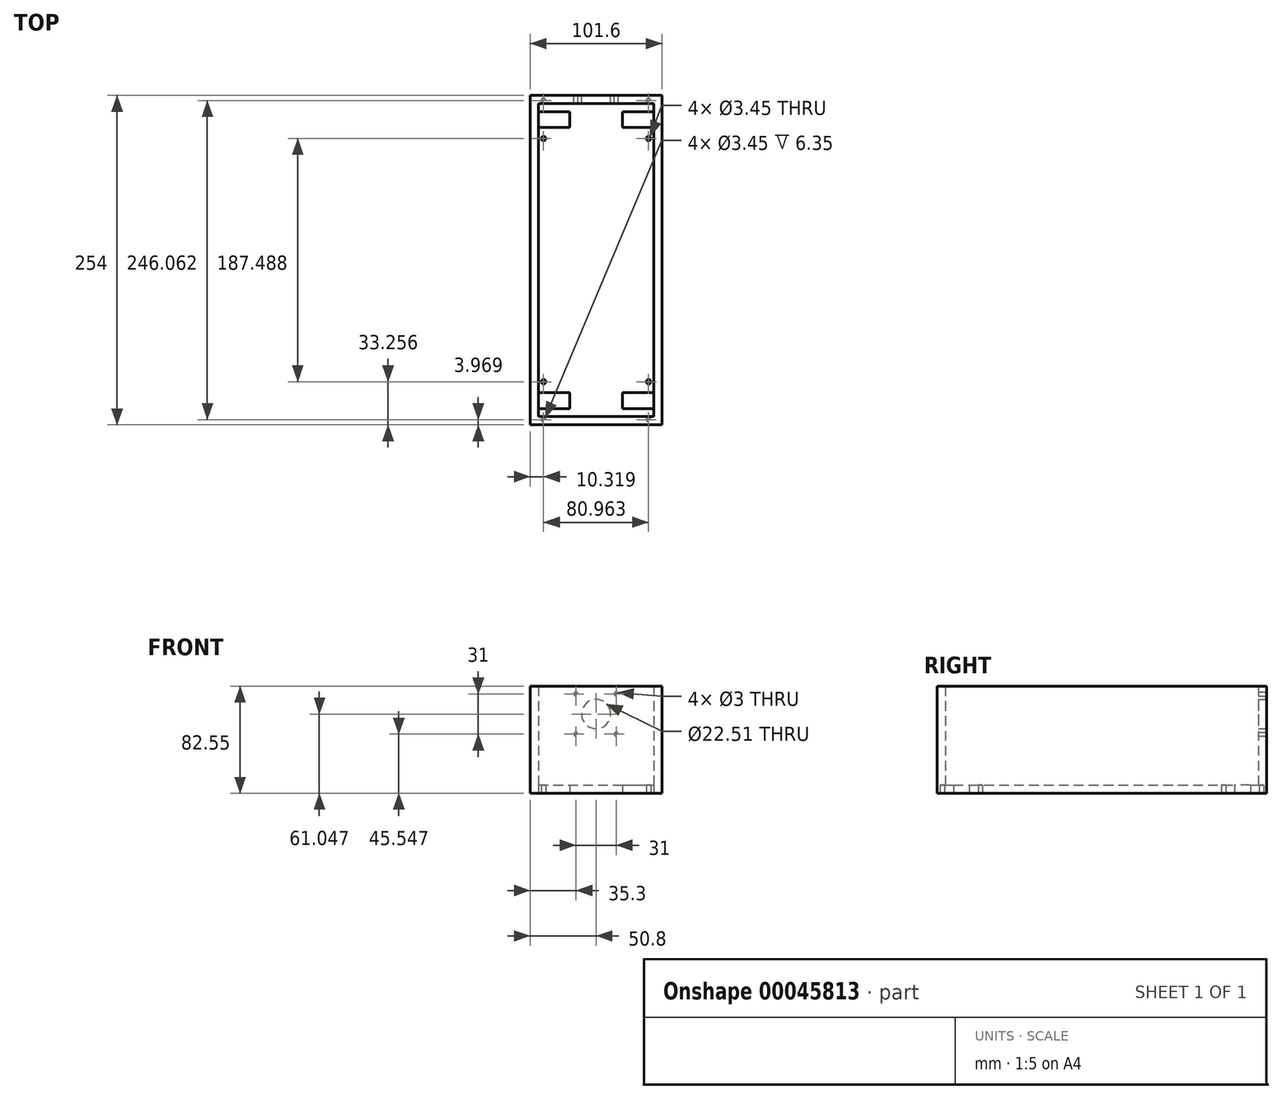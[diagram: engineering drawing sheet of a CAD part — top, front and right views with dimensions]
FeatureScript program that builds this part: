
annotation { "Feature Type Name" : "Feature", "Feature Type Description" : "" }
export const myFeature = defineFeature(function(context is Context, id is Id, definition is map)
    precondition{}
    {
        {
            var Q0;
            Q0=qCreatedBy(makeId("Top.planeOp"),FACE);
            var sketch = newSketch(context, id + "F0", { "sketchPlane" : qUnion([Q0])});
            skLineSegment(sketch, "E0.bottom", {"start": v(0, 0) * mm, "end": v(101.6, 0) * mm});
            skLineSegment(sketch, "E0.top", {"start": v(0, -254) * mm, "end": v(101.6, -254) * mm});
            skLineSegment(sketch, "E0.left", {"start": v(0, 0) * mm, "end": v(0, -254) * mm});
            skLineSegment(sketch, "E0.right", {"start": v(101.6, 0) * mm, "end": v(101.6, -254) * mm});
            skLineSegment(sketch, "E1.bottom", {"start": v(6.35, -12.49) * mm, "end": v(30.35, -12.49) * mm});
            skLineSegment(sketch, "E1.top", {"start": v(6.35, -24.74) * mm, "end": v(30.35, -24.74) * mm});
            skLineSegment(sketch, "E1.left", {"start": v(6.35, -12.49) * mm, "end": v(6.35, -24.74) * mm});
            skLineSegment(sketch, "E1.right", {"start": v(30.35, -12.49) * mm, "end": v(30.35, -24.74) * mm});
            skLineSegment(sketch, "E2.bottom", {"start": v(71.25, -12.49) * mm, "end": v(95.25, -12.49) * mm});
            skLineSegment(sketch, "E2.top", {"start": v(71.25, -24.74) * mm, "end": v(95.25, -24.74) * mm});
            skLineSegment(sketch, "E2.left", {"start": v(71.25, -12.49) * mm, "end": v(71.25, -24.74) * mm});
            skLineSegment(sketch, "E2.right", {"start": v(95.25, -12.49) * mm, "end": v(95.25, -24.74) * mm});
            skLineSegment(sketch, "E3.bottom", {"start": v(95.25, -241.51) * mm, "end": v(71.25, -241.51) * mm});
            skLineSegment(sketch, "E3.top", {"start": v(95.25, -229.26) * mm, "end": v(71.25, -229.26) * mm});
            skLineSegment(sketch, "E3.left", {"start": v(95.25, -241.51) * mm, "end": v(95.25, -229.26) * mm});
            skLineSegment(sketch, "E3.right", {"start": v(71.25, -241.51) * mm, "end": v(71.25, -229.26) * mm});
            skLineSegment(sketch, "E4.bottom", {"start": v(30.35, -241.51) * mm, "end": v(6.35, -241.51) * mm});
            skLineSegment(sketch, "E4.top", {"start": v(30.35, -229.26) * mm, "end": v(6.35, -229.26) * mm});
            skLineSegment(sketch, "E4.left", {"start": v(30.35, -241.51) * mm, "end": v(30.35, -229.26) * mm});
            skLineSegment(sketch, "E4.right", {"start": v(6.35, -241.51) * mm, "end": v(6.35, -229.26) * mm});
            skLineSegment(sketch, "E5", {"start": v(30.35, -235.39) * mm, "end": v(71.25, -235.39) * mm, "construction": true});
            skLineSegment(sketch, "E6", {"start": v(30.35, -18.61) * mm, "end": v(71.25, -18.61) * mm, "construction": true});
            skLineSegment(sketch, "E7", {"start": v(50.8, -18.61) * mm, "end": v(50.8, -235.39) * mm, "construction": true});
            skLineSegment(sketch, "E8", {"start": v(0, -127) * mm, "end": v(101.6, -127) * mm, "construction": true});
            skPoint(sketch, "E9", {"position": v(50.8, -127) * mm});
            skLineSegment(sketch, "E10.rect.bottom", {"start": v(91.28, -33.26) * mm, "end": v(10.32, -33.26) * mm, "construction": true});
            skLineSegment(sketch, "E10.rect.top", {"start": v(91.28, -3.97) * mm, "end": v(10.32, -3.97) * mm, "construction": true});
            skLineSegment(sketch, "E10.rect.left", {"start": v(91.28, -33.26) * mm, "end": v(91.28, -3.97) * mm, "construction": true});
            skLineSegment(sketch, "E10.rect.right", {"start": v(10.32, -33.26) * mm, "end": v(10.32, -3.97) * mm, "construction": true});
            skPoint(sketch, "E10.rect.middle", {"position": v(50.8, -18.61) * mm});
            skLineSegment(sketch, "E11.rect.bottom", {"start": v(91.28, -250.03) * mm, "end": v(10.32, -250.03) * mm, "construction": true});
            skLineSegment(sketch, "E11.rect.top", {"start": v(91.28, -220.74) * mm, "end": v(10.32, -220.74) * mm, "construction": true});
            skLineSegment(sketch, "E11.rect.left", {"start": v(91.28, -250.03) * mm, "end": v(91.28, -220.74) * mm, "construction": true});
            skLineSegment(sketch, "E11.rect.right", {"start": v(10.32, -250.03) * mm, "end": v(10.32, -220.74) * mm, "construction": true});
            skPoint(sketch, "E11.rect.middle", {"position": v(50.8, -235.39) * mm});
            skLineSegment(sketch, "E12", {"start": v(95.25, -12.49) * mm, "end": v(95.25, -3.97) * mm, "construction": true});
            skLineSegment(sketch, "E13", {"start": v(95.25, -3.97) * mm, "end": v(91.28, -3.97) * mm, "construction": true});
            skCircle(sketch, "E14", {"center": v(91.28, -33.26) * mm, "radius": 1.73 * mm});
            skCircle(sketch, "E15", {"center": v(91.28, -3.97) * mm, "radius": 1.73 * mm});
            skCircle(sketch, "E16", {"center": v(10.32, -3.97) * mm, "radius": 1.73 * mm});
            skCircle(sketch, "E17", {"center": v(10.32, -33.26) * mm, "radius": 1.73 * mm});
            skCircle(sketch, "E18", {"center": v(10.32, -220.74) * mm, "radius": 1.73 * mm});
            skCircle(sketch, "E19", {"center": v(10.32, -250.03) * mm, "radius": 1.73 * mm});
            skCircle(sketch, "E20", {"center": v(91.28, -250.03) * mm, "radius": 1.73 * mm});
            skCircle(sketch, "E21", {"center": v(91.28, -220.74) * mm, "radius": 1.73 * mm});
            skLineSegment(sketch, "E22", {"start": v(91.28, -3.97) * mm, "end": v(91.28, 0) * mm, "construction": true});
            skSolve(sketch);
        }
        {
            var Q0;
            Q0=qSketchRegion(id+"F0",true);
            extrude(context, id + "F1", {"entities" : qUnion([Q0]), "depth" : 6.35 * mm});
        }
        {
            var Q0;
            Q0=makeQuery(id+"F1.opExtrude","CAP_FACE",FACE,{"disambiguationData":[OSD([sQuery(id+"F0.wireOp",EDGE,"E0.bottom"),sQuery(id+"F0.wireOp",EDGE,"E0.top"),sQuery(id+"F0.wireOp",EDGE,"E0.left"),sQuery(id+"F0.wireOp",EDGE,"E0.right"),sQuery(id+"F0.wireOp",EDGE,"E1.bottom"),sQuery(id+"F0.wireOp",EDGE,"E1.top"),sQuery(id+"F0.wireOp",EDGE,"E1.left"),sQuery(id+"F0.wireOp",EDGE,"E1.right"),sQuery(id+"F0.wireOp",EDGE,"E2.bottom"),sQuery(id+"F0.wireOp",EDGE,"E2.top"),sQuery(id+"F0.wireOp",EDGE,"E2.left"),sQuery(id+"F0.wireOp",EDGE,"E2.right"),sQuery(id+"F0.wireOp",EDGE,"E3.bottom"),sQuery(id+"F0.wireOp",EDGE,"E3.top"),sQuery(id+"F0.wireOp",EDGE,"E3.left"),sQuery(id+"F0.wireOp",EDGE,"E3.right"),sQuery(id+"F0.wireOp",EDGE,"E4.bottom"),sQuery(id+"F0.wireOp",EDGE,"E4.top"),sQuery(id+"F0.wireOp",EDGE,"E4.left"),sQuery(id+"F0.wireOp",EDGE,"E4.right"),sQuery(id+"F0.wireOp",EDGE,"E14"),sQuery(id+"F0.wireOp",EDGE,"E15"),sQuery(id+"F0.wireOp",EDGE,"E16"),sQuery(id+"F0.wireOp",EDGE,"E17"),sQuery(id+"F0.wireOp",EDGE,"E18"),sQuery(id+"F0.wireOp",EDGE,"E19"),sQuery(id+"F0.wireOp",EDGE,"E20"),sQuery(id+"F0.wireOp",EDGE,"E21")])],"isStart":false});
            var sketch = newSketch(context, id + "F2", { "sketchPlane" : qUnion([Q0])});
            skLineSegment(sketch, "E23", {"start": v(0, -127) * mm, "end": v(101.6, -127) * mm, "construction": true});
            skLineSegment(sketch, "E24.rect.bottom", {"start": v(0, -254) * mm, "end": v(101.6, -254) * mm});
            skLineSegment(sketch, "E24.rect.top", {"start": v(0, 0) * mm, "end": v(101.6, 0) * mm});
            skLineSegment(sketch, "E24.rect.left", {"start": v(0, -254) * mm, "end": v(0, 0) * mm});
            skLineSegment(sketch, "E24.rect.right", {"start": v(101.6, -254) * mm, "end": v(101.6, 0) * mm});
            skPoint(sketch, "E24.rect.middle", {"position": v(50.8, -127) * mm});
            skLineSegment(sketch, "E25.rect.bottom", {"start": v(6.35, -247.65) * mm, "end": v(95.25, -247.65) * mm});
            skLineSegment(sketch, "E25.rect.top", {"start": v(6.35, -6.35) * mm, "end": v(95.25, -6.35) * mm});
            skLineSegment(sketch, "E25.rect.left", {"start": v(6.35, -247.65) * mm, "end": v(6.35, -6.35) * mm});
            skLineSegment(sketch, "E25.rect.right", {"start": v(95.25, -247.65) * mm, "end": v(95.25, -6.35) * mm});
            skLineSegment(sketch, "E26", {"start": v(50.8, -247.65) * mm, "end": v(50.8, -254) * mm, "construction": true});
            skSolve(sketch);
        }
        {
            var Q0;
            Q0=qSketchRegion(id+"F2",true);
            extrude(context, id + "F3", {"entities" : qUnion([Q0]), "operationType" : NewBodyOperationType.ADD, "depth" : 76.2 * mm});
        }
        {
            var Q0;
            Q0=makeQuery(id+"F3.boolean.opBoolean","MERGE",FACE,{"derivedFrom":[makeQuery(id+"F1.opExtrude","SWEPT_FACE",FACE,{"disambiguationData":[OSD([sQuery(id+"F0.wireOp",EDGE,"E0.bottom")])]}),makeQuery(id+"F3.opExtrude","SWEPT_FACE",FACE,{"disambiguationData":[OSD([sQuery(id+"F2.wireOp",EDGE,"E24.rect.top")])]})]});
            var sketch = newSketch(context, id + "F4", { "sketchPlane" : qUnion([Q0])});
            skLineSegment(sketch, "E27", {"start": v(-50.8, 82.55) * mm, "end": v(-50.8, 61.05) * mm, "construction": true});
            skLineSegment(sketch, "E28.rect.bottom", {"start": v(-35.3, 76.55) * mm, "end": v(-66.3, 76.55) * mm, "construction": true});
            skLineSegment(sketch, "E28.rect.top", {"start": v(-35.3, 45.55) * mm, "end": v(-66.3, 45.55) * mm, "construction": true});
            skLineSegment(sketch, "E28.rect.left", {"start": v(-35.3, 76.55) * mm, "end": v(-35.3, 45.55) * mm, "construction": true});
            skLineSegment(sketch, "E28.rect.right", {"start": v(-66.3, 76.55) * mm, "end": v(-66.3, 45.55) * mm, "construction": true});
            skPoint(sketch, "E28.rect.middle", {"position": v(-50.8, 61.05) * mm});
            skCircle(sketch, "E29", {"center": v(-66.3, 76.55) * mm, "radius": 1.5 * mm});
            skCircle(sketch, "E30", {"center": v(-35.3, 76.55) * mm, "radius": 1.5 * mm});
            skCircle(sketch, "E31", {"center": v(-66.3, 45.55) * mm, "radius": 1.5 * mm});
            skCircle(sketch, "E32", {"center": v(-50.8, 61.05) * mm, "radius": 11.25 * mm});
            skCircle(sketch, "E33", {"center": v(-35.3, 45.55) * mm, "radius": 1.5 * mm});
            skSolve(sketch);
        }
        {
            var Q0;
            Q0=qSketchRegion(id+"F4",true);
            var Q1;
            Q1=makeQuery(id+"F3.opExtrude","SWEPT_FACE",FACE,{"disambiguationData":[OSD([sQuery(id+"F2.wireOp",EDGE,"E25.rect.top")])]});
            extrude(context, id + "F5", {"entities" : qUnion([Q0]), "operationType" : NewBodyOperationType.REMOVE, "endBound" : BoundingType.UP_TO_SURFACE, "oppositeDirection" : true, "endBoundEntityFace" : qUnion([Q1]), "depth" : 25.4 * mm});
        }
        {
            var Q0;
            Q0=qSketchRegion(id+"F4",true);
            var Q1;
            Q1=makeQuery(id+"F3.opExtrude","SWEPT_FACE",FACE,{"disambiguationData":[OSD([sQuery(id+"F2.wireOp",EDGE,"E25.rect.top")])]});
            extrude(context, id + "F6", {"entities" : qUnion([Q0]), "operationType" : NewBodyOperationType.REMOVE, "endBound" : BoundingType.UP_TO_SURFACE, "oppositeDirection" : true, "endBoundEntityFace" : qUnion([Q1]), "depth" : 25.4 * mm});
        }
    });
